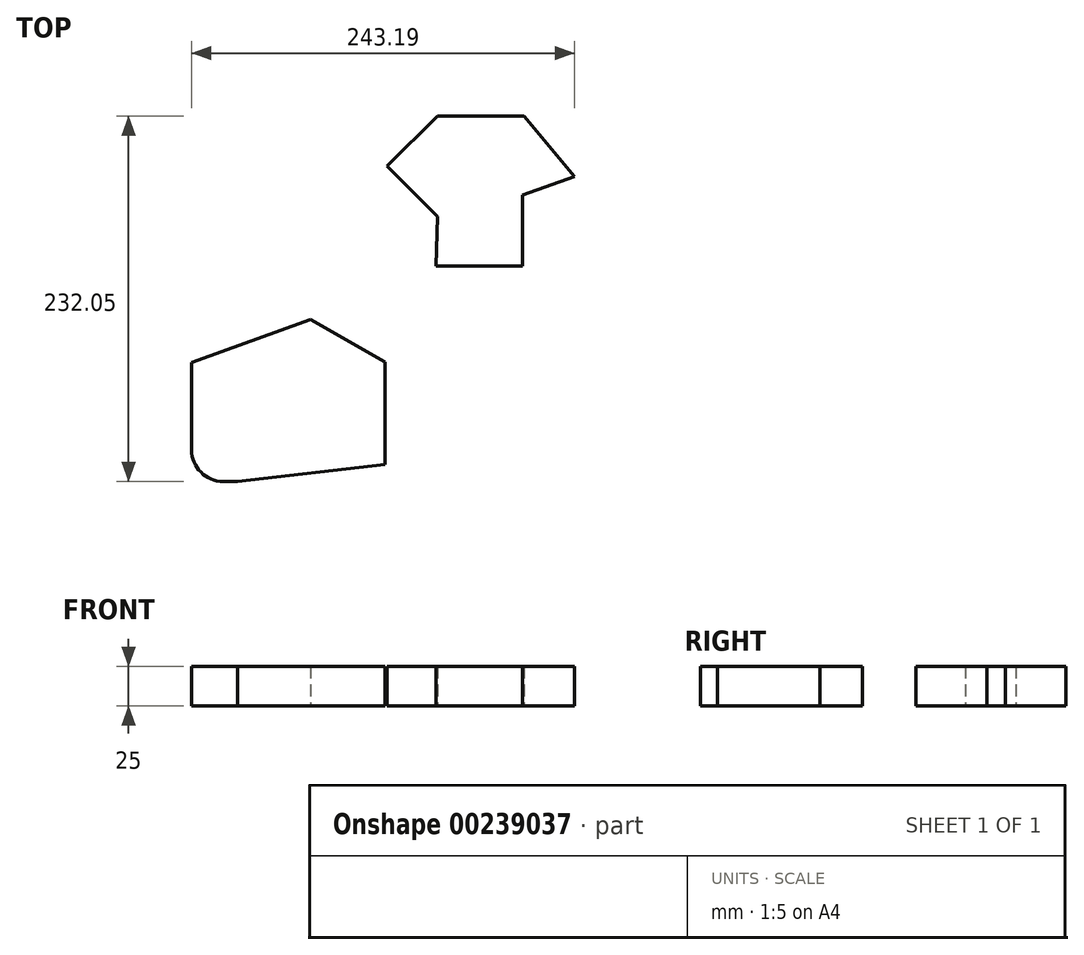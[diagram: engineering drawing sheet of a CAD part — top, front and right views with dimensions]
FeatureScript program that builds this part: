
annotation { "Feature Type Name" : "Feature", "Feature Type Description" : "" }
export const myFeature = defineFeature(function(context is Context, id is Id, definition is map)
    precondition{}
    {
        {
            var Q0;
            Q0=qCreatedBy(makeId("Top.planeOp"),FACE);
            var sketch = newSketch(context, id + "F0", { "sketchPlane" : qUnion([Q0])});
            skLineSegment(sketch, "E0", {"start": v(-34.45, -32.1) * mm, "end": v(20.55, -32.1) * mm});
            skLineSegment(sketch, "E1", {"start": v(20.55, -32.1) * mm, "end": v(20.55, 12.9) * mm});
            skLineSegment(sketch, "E2", {"start": v(20.55, 12.9) * mm, "end": v(53.43, 24.88) * mm});
            skLineSegment(sketch, "E3", {"start": v(53.43, 24.88) * mm, "end": v(12.23, 24.88) * mm, "construction": true});
            skLineSegment(sketch, "E4", {"start": v(53.43, 24.88) * mm, "end": v(21.3, 63.18) * mm});
            skLineSegment(sketch, "E5", {"start": v(21.3, 63.18) * mm, "end": v(-33.7, 63.18) * mm});
            skLineSegment(sketch, "E6", {"start": v(-33.7, 63.18) * mm, "end": v(-65.52, 31.36) * mm});
            skLineSegment(sketch, "E7", {"start": v(-65.52, 31.36) * mm, "end": v(-33.7, -0.46) * mm});
            skLineSegment(sketch, "E8", {"start": v(-22.37, 31.36) * mm, "end": v(-65.52, 31.36) * mm});
            skLineSegment(sketch, "E9", {"start": v(-34.45, -32.1) * mm, "end": v(-33.7, -0.46) * mm});
            skLineSegment(sketch, "E10", {"start": v(-66.95, -93.12) * mm, "end": v(-66.95, -158.12) * mm});
            skLineSegment(sketch, "E11", {"start": v(-66.95, -93.12) * mm, "end": v(-108.15, -93.12) * mm, "construction": true});
            skLineSegment(sketch, "E12", {"start": v(-66.95, -93.12) * mm, "end": v(-114.16, -65.86) * mm});
            skLineSegment(sketch, "E13", {"start": v(-114.16, -65.86) * mm, "end": v(-189.76, -93.38) * mm});
            skLineSegment(sketch, "E14", {"start": v(-189.76, -93.38) * mm, "end": v(-189.76, -148.87) * mm});
            skLineSegment(sketch, "E15", {"start": v(-189.76, -93.38) * mm, "end": v(-148.24, -93.38) * mm, "construction": true});
            skLineSegment(sketch, "E16", {"start": v(-169.76, -168.87) * mm, "end": v(-160.49, -168.87) * mm});
            skPoint(sketch, "E17.visualSharp", {"position": v(-189.76, -168.87) * mm});
            skArc(sketch, "E17.filletArc", {"start": v(-189.76, -148.87) * mm, "mid": v(-183.9, -163) * mm, "end": v(-169.76, -168.87) * mm});
            skLineSegment(sketch, "E18", {"start": v(-66.95, -158.12) * mm, "end": v(-160.49, -168.87) * mm});
            skSolve(sketch);
        }
        {
            var Q0;
            Q0=makeQuery(id+"F0.imprint","IMPRINT",FACE,{"disambiguationData":[TD([[makeQuery(id+"F0.imprint","IMPRINT",EDGE,{"derivedFrom":sQuery(id+"F0.wireOp",EDGE,"E0")}),1.0]])]});
            extrude(context, id + "F1", {"entities" : qUnion([Q0]), "depth" : 25 * mm});
        }
        {
            var Q0;
            Q0=makeQuery(id+"F0.imprint","IMPRINT",FACE,{"disambiguationData":[TD([[makeQuery(id+"F0.imprint","IMPRINT",EDGE,{"derivedFrom":sQuery(id+"F0.wireOp",EDGE,"E10")}),-1.0]])]});
            extrude(context, id + "F2", {"entities" : qUnion([Q0]), "depth" : 25 * mm});
        }
    });
